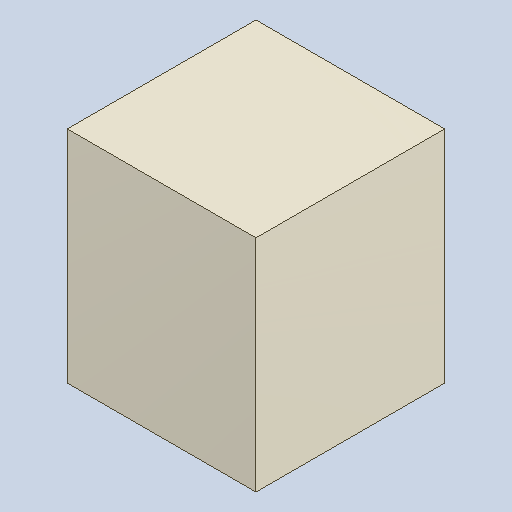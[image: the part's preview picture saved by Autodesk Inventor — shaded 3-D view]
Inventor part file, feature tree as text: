
AUTODESK INVENTOR PART (.ipt)
format: ipt  version: 2023.4 (Build 274418000, 418)  size: 82,944 bytes
history: native  units: mm
features: extrude x1
ambient origin geometry x8: Origin, YZ Plane, XZ Plane, XY Plane, X Axis, Y Axis, Z Axis, Center Point
bodies: Solid1 (feature_tree)
feature tree (1):
  extrude  "Extruded_29"  [1 undecoded]
note: 1 required parameter value undecoded (feature->parameter linkage not recoverable at this tier; creation-order binding heuristic only, values carry confidence <= 0.55)
